# Revit family: MUTE_DESIGN_SPACE L
name_source: partatom
category: Modele ogólne
revit_build: Autodesk Revit 2017 (Build: 20160720_1515(x64)
units: mm (PartAtom-declared; Revit-internal decimal feet)

## family parameters
Może być obiektem nadrzędnym dla zbrojenia = Nie
Oparty na płaszczyźnie roboczej = Nie
Punkt obliczania pomieszczeń = Nie
Tnij formami wycięć po wczytaniu = Nie
Typ części = Normalny
Współdzielony = Nie
Wymiar okrągłego złącza = Użyj średnicy
Zawsze pionowo = Tak

## types (1)
- MUTE_DESIGN_SPACE L
    Autor = www.archispace.pl
    Filc = Mute_Design - Szary
    Głębokość = 1305 mm  [stored 4.2815 ft]
    Link do karty produktu = https://mutedesign.ovh
    Link do strony produktu = hthttps://mute.design
    Materiał_blat = MUTE_DESIGN_domyślny
    Materiał_kanapa = MUTE_DESIGN_domyślny
    Materiał_klamka = Mute_Design - Rurka/klamka/noga_hoker - Szary
    Materiał_przeszklenia = MUTE_DESIGN_Szkło
    Materiał_rama = MUTE_DESIGN_domyślny
    Materiał_ściany_i_dach = MUTE_DESIGN_domyślny
    Model = SPACE L
    Producent = MuteDesign
    Szerokość = 2200 mm
    URL = https://mute.design
    Wysokość = 2247 mm  [stored 7.37205 ft]

note: [stored X ft] marks values corroborated as IEEE doubles in the binary element streams (Revit-internal decimal feet)
